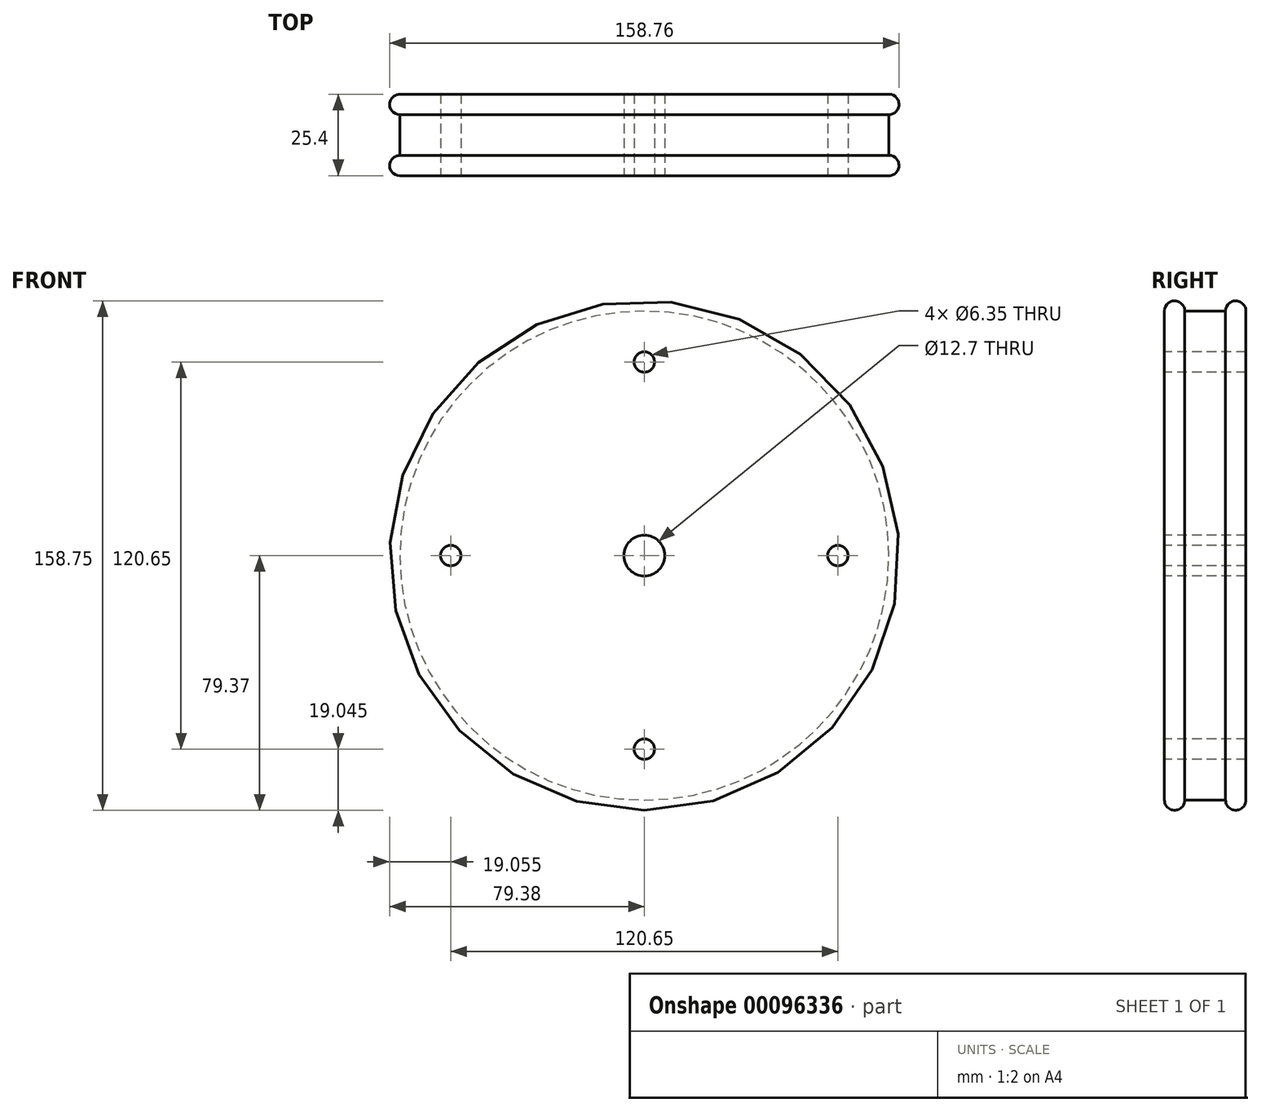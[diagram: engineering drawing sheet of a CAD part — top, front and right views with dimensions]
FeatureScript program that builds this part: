
annotation { "Feature Type Name" : "Feature", "Feature Type Description" : "" }
export const myFeature = defineFeature(function(context is Context, id is Id, definition is map)
    precondition{}
    {
        {
            var Q0;
            Q0=qCreatedBy(makeId("Front.planeOp"),FACE);
            var sketch = newSketch(context, id + "F0", { "sketchPlane" : qUnion([Q0])});
            skCircle(sketch, "E0", {"center": v(0, 0) * mm, "radius": 79.38 * mm});
            skSolve(sketch);
        }
        {
            var Q0;
            Q0 = qSketchRegion(id + "F0", true);
            extrude(context, id + "F1", {"entities" : qUnion([Q0]), "depth" : 6.35 * mm});
        }
        {
            var Q0;
            Q0=makeQuery(id+"F1.opExtrude","CAP_FACE",FACE,{"disambiguationData":[OSD([sQuery(id+"F0.wireOp",EDGE,"E0")])],"isStart":false});
            var sketch = newSketch(context, id + "F2", { "sketchPlane" : qUnion([Q0])});
            skCircle(sketch, "E1", {"center": v(0, 0) * mm, "radius": 76.2 * mm});
            skSolve(sketch);
        }
        {
            var Q0;
            Q0 = qSketchRegion(id + "F2", true);
            extrude(context, id + "F3", {"entities" : qUnion([Q0]), "operationType" : NewBodyOperationType.ADD, "depth" : 12.7 * mm});
        }
        {
            var Q0;
            Q0=makeQuery(id+"F1.opExtrude","SWEPT_FACE",FACE,{"disambiguationData":[OSD([sQuery(id+"F0.wireOp",EDGE,"E0")])]});
            fillet(context, id + "F4", {"entities" : qUnion([Q0]), "radius" : 3.17 * mm, "tangentPropagation" : true, "allowEdgeOverflow" : false});
        }
        {
            var Q0;
            Q0=makeQuery(id+"F3.opExtrude","CAP_FACE",FACE,{"disambiguationData":[OSD([sQuery(id+"F2.wireOp",EDGE,"E1")])],"isStart":false});
            var sketch = newSketch(context, id + "F5", { "sketchPlane" : qUnion([Q0])});
            skCircle(sketch, "E2", {"center": v(0, 0) * mm, "radius": 79.37 * mm});
            skSolve(sketch);
        }
        {
            var Q0;
            Q0 = qSketchRegion(id + "F5", true);
            extrude(context, id + "F6", {"entities" : qUnion([Q0]), "operationType" : NewBodyOperationType.ADD, "depth" : 6.35 * mm});
        }
        {
            var Q0;
            Q0=makeQuery(id+"F6.opExtrude","SWEPT_FACE",FACE,{"disambiguationData":[OSD([sQuery(id+"F5.wireOp",EDGE,"E2")])]});
            fillet(context, id + "F7", {"entities" : qUnion([Q0]), "radius" : 3.17 * mm, "tangentPropagation" : true, "allowEdgeOverflow" : false});
        }
        {
            var Q0;
            Q0=makeQuery(id+"F6.opExtrude","CAP_FACE",FACE,{"disambiguationData":[OSD([sQuery(id+"F5.wireOp",EDGE,"E2")])],"isStart":false});
            var sketch = newSketch(context, id + "F8", { "sketchPlane" : qUnion([Q0])});
            skCircle(sketch, "E3", {"center": v(0, 0) * mm, "radius": 6.35 * mm});
            skCircle(sketch, "E4", {"center": v(-60.32, 0) * mm, "radius": 3.17 * mm});
            skCircle(sketch, "E5", {"center": v(0, 60.32) * mm, "radius": 3.18 * mm});
            skCircle(sketch, "E6", {"center": v(60.32, 0) * mm, "radius": 3.18 * mm});
            skCircle(sketch, "E7", {"center": v(0, -60.32) * mm, "radius": 3.18 * mm});
            skSolve(sketch);
        }
        {
            var Q0;
            Q0 = qSketchRegion(id + "F8", true);
            extrude(context, id + "F9", {"entities" : qUnion([Q0]), "operationType" : NewBodyOperationType.REMOVE, "endBound" : BoundingType.THROUGH_ALL, "oppositeDirection" : true, "depth" : 25.4 * mm});
        }
    });
